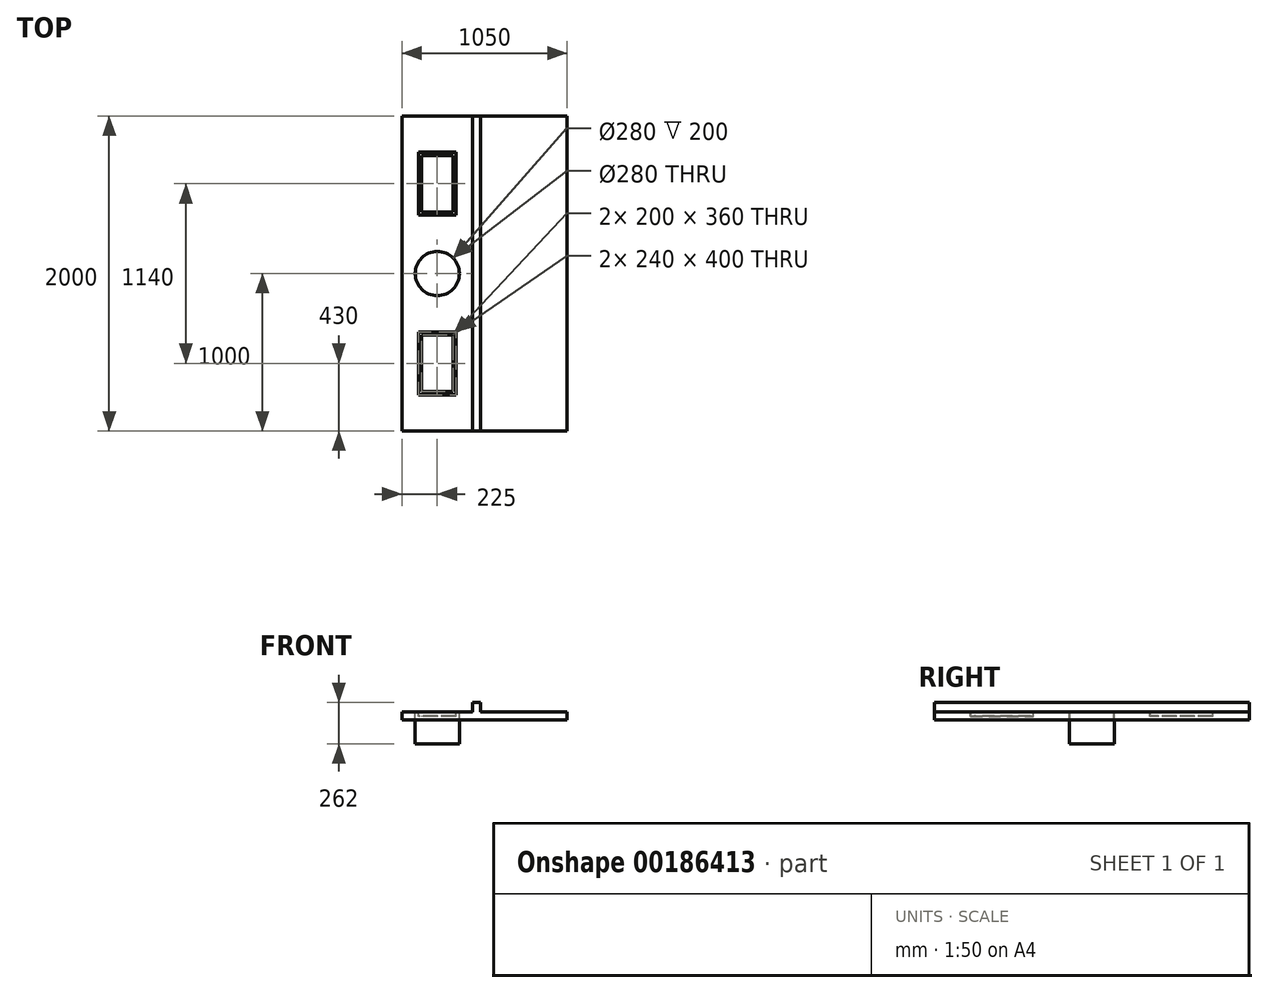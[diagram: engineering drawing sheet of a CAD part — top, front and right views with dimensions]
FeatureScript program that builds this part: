
annotation { "Feature Type Name" : "Feature", "Feature Type Description" : "" }
export const myFeature = defineFeature(function(context is Context, id is Id, definition is map)
    precondition{}
    {
        {
            var Q0;
            Q0=qCreatedBy(makeId("Front.planeOp"),FACE);
            var sketch = newSketch(context, id + "F0", { "sketchPlane" : qUnion([Q0])});
            skLineSegment(sketch, "E0", {"start": v(0, 0) * mm, "end": v(0, 50) * mm});
            skLineSegment(sketch, "E1", {"start": v(0, 50) * mm, "end": v(450, 50) * mm});
            skLineSegment(sketch, "E2", {"start": v(450, 50) * mm, "end": v(450, 110) * mm});
            skLineSegment(sketch, "E3", {"start": v(450, 110) * mm, "end": v(500, 110) * mm});
            skLineSegment(sketch, "E4", {"start": v(500, 110) * mm, "end": v(500, 50) * mm});
            skLineSegment(sketch, "E5", {"start": v(500, 50) * mm, "end": v(1050, 50) * mm});
            skLineSegment(sketch, "E6", {"start": v(1050, 50) * mm, "end": v(1050, 0) * mm});
            skLineSegment(sketch, "E7", {"start": v(0, 0) * mm, "end": v(2, 0) * mm});
            skLineSegment(sketch, "E8", {"start": v(2, 0) * mm, "end": v(2, 48) * mm});
            skLineSegment(sketch, "E9", {"start": v(2, 48) * mm, "end": v(452, 48) * mm});
            skLineSegment(sketch, "E10", {"start": v(452, 48) * mm, "end": v(452, 108) * mm});
            skLineSegment(sketch, "E11", {"start": v(452, 108) * mm, "end": v(498, 108) * mm});
            skLineSegment(sketch, "E12", {"start": v(498, 108) * mm, "end": v(498, 48) * mm});
            skLineSegment(sketch, "E13", {"start": v(498, 48) * mm, "end": v(1048, 48) * mm});
            skLineSegment(sketch, "E14", {"start": v(1048, 48) * mm, "end": v(1048, 0) * mm});
            skLineSegment(sketch, "E15", {"start": v(1048, 0) * mm, "end": v(1050, 0) * mm});
            skSolve(sketch);
        }
        {
            var Q0;
            Q0 = qSketchRegion(id + "F0", true);
            extrude(context, id + "F1", {"entities" : qUnion([Q0]), "depth" : 2000 * mm});
        }
        {
            var Q0;
            Q0=makeQuery(id+"F1.opExtrude","SWEPT_FACE",FACE,{"disambiguationData":[OSD([sQuery(id+"F0.wireOp",EDGE,"E1")])]});
            var sketch = newSketch(context, id + "F2", { "sketchPlane" : qUnion([Q0])});
            skCircle(sketch, "E16", {"center": v(225, -1000) * mm, "radius": 140 * mm});
            skPoint(sketch, "E16.centerSnap0", {"position": v(225, 0) * mm});
            skPoint(sketch, "E16.centerSnap1", {"position": v(0, -1000) * mm});
            skLineSegment(sketch, "E17.bottom", {"start": v(345, -230) * mm, "end": v(105, -230) * mm});
            skLineSegment(sketch, "E17.top", {"start": v(345, -630) * mm, "end": v(105, -630) * mm});
            skLineSegment(sketch, "E17.left", {"start": v(345, -230) * mm, "end": v(345, -630) * mm});
            skLineSegment(sketch, "E17.right", {"start": v(105, -230) * mm, "end": v(105, -630) * mm});
            skPoint(sketch, "E17.middle", {"position": v(225, -430) * mm});
            skLineSegment(sketch, "E18.bottom", {"start": v(345, -1770) * mm, "end": v(105, -1770) * mm});
            skLineSegment(sketch, "E18.top", {"start": v(345, -1370) * mm, "end": v(105, -1370) * mm});
            skLineSegment(sketch, "E18.left", {"start": v(345, -1770) * mm, "end": v(345, -1370) * mm});
            skLineSegment(sketch, "E18.right", {"start": v(105, -1770) * mm, "end": v(105, -1370) * mm});
            skPoint(sketch, "E18.middle", {"position": v(225, -1570) * mm});
            skSolve(sketch);
        }
        {
            var Q0;
            Q0 = qSketchRegion(id + "F2", true);
            extrude(context, id + "F3", {"entities" : qUnion([Q0]), "operationType" : NewBodyOperationType.REMOVE, "oppositeDirection" : true, "depth" : 25 * mm});
        }
        {
            var Q0;
            Q0=makeQuery(id+"F1.opExtrude","SWEPT_FACE",FACE,{"disambiguationData":[OSD([sQuery(id+"F0.wireOp",EDGE,"E9")])]});
            var sketch = newSketch(context, id + "F4", { "sketchPlane" : qUnion([Q0])});
            skLineSegment(sketch, "E19.bottom", {"start": v(105, 630) * mm, "end": v(345, 630) * mm});
            skLineSegment(sketch, "E19.top", {"start": v(105, 230) * mm, "end": v(345, 230) * mm});
            skLineSegment(sketch, "E19.left", {"start": v(105, 630) * mm, "end": v(105, 230) * mm});
            skLineSegment(sketch, "E19.right", {"start": v(345, 630) * mm, "end": v(345, 230) * mm});
            skPoint(sketch, "E19.middle", {"position": v(225, 430) * mm});
            skPoint(sketch, "E19.middle.positionSnap0", {"position": v(225, 230) * mm});
            skPoint(sketch, "E19.middle.positionSnap1", {"position": v(105, 430) * mm});
            skPoint(sketch, "E19.centerSnap0", {"position": v(225, 230) * mm});
            skPoint(sketch, "E19.centerSnap1", {"position": v(105, 430) * mm});
            skLineSegment(sketch, "E20.bottom", {"start": v(105, 1770) * mm, "end": v(345, 1770) * mm});
            skLineSegment(sketch, "E20.top", {"start": v(105, 1370) * mm, "end": v(345, 1370) * mm});
            skLineSegment(sketch, "E20.left", {"start": v(105, 1770) * mm, "end": v(105, 1370) * mm});
            skLineSegment(sketch, "E20.right", {"start": v(345, 1770) * mm, "end": v(345, 1370) * mm});
            skPoint(sketch, "E20.middle", {"position": v(225, 1570) * mm});
            skPoint(sketch, "E20.middle.positionSnap0", {"position": v(105, 1570) * mm});
            skPoint(sketch, "E20.middle.positionSnap1", {"position": v(225, 1370) * mm});
            skPoint(sketch, "E20.centerSnap0", {"position": v(105, 1570) * mm});
            skPoint(sketch, "E20.centerSnap1", {"position": v(225, 1370) * mm});
            skSolve(sketch);
        }
        {
            var Q0;
            Q0 = qSketchRegion(id + "F4", true);
            extrude(context, id + "F5", {"entities" : qUnion([Q0]), "depth" : 25 * mm});
        }
        {
            var Q0;
            Q0=makeQuery(id+"F5.opExtrude","CAP_FACE",FACE,{"disambiguationData":[OSD([sQuery(id+"F4.wireOp",EDGE,"E19.bottom"),sQuery(id+"F4.wireOp",EDGE,"E19.top"),sQuery(id+"F4.wireOp",EDGE,"E19.left"),sQuery(id+"F4.wireOp",EDGE,"E19.right")])],"isStart":true});
            var Q1;
            Q1=makeQuery(id+"F5.opExtrude","CAP_FACE",FACE,{"disambiguationData":[OSD([sQuery(id+"F4.wireOp",EDGE,"E20.bottom"),sQuery(id+"F4.wireOp",EDGE,"E20.top"),sQuery(id+"F4.wireOp",EDGE,"E20.left"),sQuery(id+"F4.wireOp",EDGE,"E20.right")])],"isStart":true});
            shell(context, id + "F6", {"entities" : qUnion([Q0, Q1]), "thickness" : 2 * mm});
        }
        {
            var Q0;
            Q0=makeQuery(id+"F5.opExtrude","CAP_FACE",FACE,{"disambiguationData":[OSD([sQuery(id+"F4.wireOp",EDGE,"E19.bottom"),sQuery(id+"F4.wireOp",EDGE,"E19.top"),sQuery(id+"F4.wireOp",EDGE,"E19.left"),sQuery(id+"F4.wireOp",EDGE,"E19.right")])],"isStart":false});
            var sketch = newSketch(context, id + "F7", { "sketchPlane" : qUnion([Q0])});
            skLineSegment(sketch, "E21.bottom", {"start": v(325, 250) * mm, "end": v(125, 250) * mm});
            skLineSegment(sketch, "E21.top", {"start": v(325, 610) * mm, "end": v(125, 610) * mm});
            skLineSegment(sketch, "E21.left", {"start": v(325, 250) * mm, "end": v(325, 610) * mm});
            skLineSegment(sketch, "E21.right", {"start": v(125, 250) * mm, "end": v(125, 610) * mm});
            skPoint(sketch, "E21.middle", {"position": v(225, 430) * mm});
            skPoint(sketch, "E21.middle.positionSnap0", {"position": v(225, 630) * mm});
            skPoint(sketch, "E21.middle.positionSnap1", {"position": v(345, 430) * mm});
            skPoint(sketch, "E21.centerSnap0", {"position": v(225, 630) * mm});
            skPoint(sketch, "E21.centerSnap1", {"position": v(345, 430) * mm});
            skLineSegment(sketch, "E22.bottom", {"start": v(325, 1390) * mm, "end": v(125, 1390) * mm});
            skLineSegment(sketch, "E22.top", {"start": v(325, 1750) * mm, "end": v(125, 1750) * mm});
            skLineSegment(sketch, "E22.left", {"start": v(325, 1390) * mm, "end": v(325, 1750) * mm});
            skLineSegment(sketch, "E22.right", {"start": v(125, 1390) * mm, "end": v(125, 1750) * mm});
            skPoint(sketch, "E22.middle", {"position": v(225, 1570) * mm});
            skPoint(sketch, "E22.middle.positionSnap0", {"position": v(225, 610) * mm});
            skPoint(sketch, "E22.centerSnap0", {"position": v(225, 610) * mm});
            skSolve(sketch);
        }
        {
            var Q0;
            Q0=makeQuery(id+"F7.imprint","IMPRINT",FACE,{"disambiguationData":[TD([[makeQuery(id+"F7.imprint","IMPRINT",EDGE,{"derivedFrom":sQuery(id+"F7.wireOp",EDGE,"E21.bottom")}),-1.0]])]});
            var Q1;
            Q1=makeQuery(id+"F7.imprint","IMPRINT",FACE,{"disambiguationData":[TD([[makeQuery(id+"F7.imprint","IMPRINT",EDGE,{"derivedFrom":sQuery(id+"F7.wireOp",EDGE,"E22.bottom")}),-1.0]])]});
            extrude(context, id + "F8", {"entities" : qUnion([Q0, Q1]), "operationType" : NewBodyOperationType.REMOVE, "oppositeDirection" : true, "depth" : 25 * mm});
        }
        {
            var Q0;
            Q0=makeQuery(id+"F1.opExtrude","SWEPT_FACE",FACE,{"disambiguationData":[OSD([sQuery(id+"F0.wireOp",EDGE,"E9")])]});
            var sketch = newSketch(context, id + "F9", { "sketchPlane" : qUnion([Q0])});
            skCircle(sketch, "E23", {"center": v(225, 1000) * mm, "radius": 142 * mm});
            skSolve(sketch);
        }
        {
            var Q0;
            Q0 = qSketchRegion(id + "F9", true);
            extrude(context, id + "F10", {"entities" : qUnion([Q0]), "depth" : 200 * mm});
        }
        {
            var Q0;
            Q0=makeQuery(id+"F10.opExtrude","CAP_FACE",FACE,{"disambiguationData":[OSD([sQuery(id+"F9.wireOp",EDGE,"E23")])],"isStart":true});
            var Q1;
            Q1=makeQuery(id+"F10.opExtrude","CAP_FACE",FACE,{"disambiguationData":[OSD([sQuery(id+"F9.wireOp",EDGE,"E23")])],"isStart":false});
            shell(context, id + "F11", {"entities" : qUnion([Q0, Q1]), "thickness" : 2 * mm});
        }
        {
            var Q0;
            Q0=makeQuery(id+"F1.opExtrude","CAP_FACE",FACE,{"disambiguationData":[OSD([sQuery(id+"F0.wireOp",EDGE,"E0"),sQuery(id+"F0.wireOp",EDGE,"E1"),sQuery(id+"F0.wireOp",EDGE,"E2"),sQuery(id+"F0.wireOp",EDGE,"E3"),sQuery(id+"F0.wireOp",EDGE,"E4"),sQuery(id+"F0.wireOp",EDGE,"E5"),sQuery(id+"F0.wireOp",EDGE,"E6"),sQuery(id+"F0.wireOp",EDGE,"E7"),sQuery(id+"F0.wireOp",EDGE,"E8"),sQuery(id+"F0.wireOp",EDGE,"E9"),sQuery(id+"F0.wireOp",EDGE,"E10"),sQuery(id+"F0.wireOp",EDGE,"E11"),sQuery(id+"F0.wireOp",EDGE,"E12"),sQuery(id+"F0.wireOp",EDGE,"E13"),sQuery(id+"F0.wireOp",EDGE,"E14"),sQuery(id+"F0.wireOp",EDGE,"E15")])],"isStart":true});
            var sketch = newSketch(context, id + "F12", { "sketchPlane" : qUnion([Q0])});
            skLineSegment(sketch, "E24", {"start": v(-1050, 0) * mm, "end": v(-1050, 50) * mm});
            skLineSegment(sketch, "E25", {"start": v(-1050, 50) * mm, "end": v(-500, 50) * mm});
            skLineSegment(sketch, "E26", {"start": v(-500, 50) * mm, "end": v(-500, 110) * mm});
            skLineSegment(sketch, "E27", {"start": v(-500, 110) * mm, "end": v(-450, 110) * mm});
            skLineSegment(sketch, "E28", {"start": v(-450, 110) * mm, "end": v(-450, 50) * mm});
            skLineSegment(sketch, "E29", {"start": v(-450, 50) * mm, "end": v(0, 50) * mm});
            skLineSegment(sketch, "E30", {"start": v(0, 50) * mm, "end": v(0, 0) * mm});
            skLineSegment(sketch, "E31", {"start": v(0, 0) * mm, "end": v(-1050, 0) * mm});
            skSolve(sketch);
        }
        {
            var Q0;
            Q0 = qSketchRegion(id + "F12", true);
            extrude(context, id + "F13", {"entities" : qUnion([Q0]), "operationType" : NewBodyOperationType.ADD, "oppositeDirection" : true, "depth" : 2 * mm});
        }
        {
            var Q0;
            Q0=makeQuery(id+"F1.opExtrude","CAP_FACE",FACE,{"disambiguationData":[OSD([sQuery(id+"F0.wireOp",EDGE,"E0"),sQuery(id+"F0.wireOp",EDGE,"E1"),sQuery(id+"F0.wireOp",EDGE,"E2"),sQuery(id+"F0.wireOp",EDGE,"E3"),sQuery(id+"F0.wireOp",EDGE,"E4"),sQuery(id+"F0.wireOp",EDGE,"E5"),sQuery(id+"F0.wireOp",EDGE,"E6"),sQuery(id+"F0.wireOp",EDGE,"E7"),sQuery(id+"F0.wireOp",EDGE,"E8"),sQuery(id+"F0.wireOp",EDGE,"E9"),sQuery(id+"F0.wireOp",EDGE,"E10"),sQuery(id+"F0.wireOp",EDGE,"E11"),sQuery(id+"F0.wireOp",EDGE,"E12"),sQuery(id+"F0.wireOp",EDGE,"E13"),sQuery(id+"F0.wireOp",EDGE,"E14"),sQuery(id+"F0.wireOp",EDGE,"E15")])],"isStart":false});
            var sketch = newSketch(context, id + "F14", { "sketchPlane" : qUnion([Q0])});
            skLineSegment(sketch, "E32", {"start": v(0, 0) * mm, "end": v(0, 50) * mm});
            skLineSegment(sketch, "E33", {"start": v(0, 50) * mm, "end": v(450, 50) * mm});
            skLineSegment(sketch, "E34", {"start": v(450, 50) * mm, "end": v(450, 110) * mm});
            skLineSegment(sketch, "E35", {"start": v(450, 110) * mm, "end": v(500, 110) * mm});
            skLineSegment(sketch, "E36", {"start": v(500, 110) * mm, "end": v(500, 50) * mm});
            skLineSegment(sketch, "E37", {"start": v(500, 50) * mm, "end": v(1050, 50) * mm});
            skLineSegment(sketch, "E38", {"start": v(1050, 50) * mm, "end": v(1050, 0) * mm});
            skLineSegment(sketch, "E39", {"start": v(1050, 0) * mm, "end": v(0, 0) * mm});
            skSolve(sketch);
        }
        {
            var Q0;
            Q0 = qSketchRegion(id + "F14", true);
            extrude(context, id + "F15", {"entities" : qUnion([Q0]), "operationType" : NewBodyOperationType.ADD, "oppositeDirection" : true, "depth" : 2 * mm});
        }
    });
